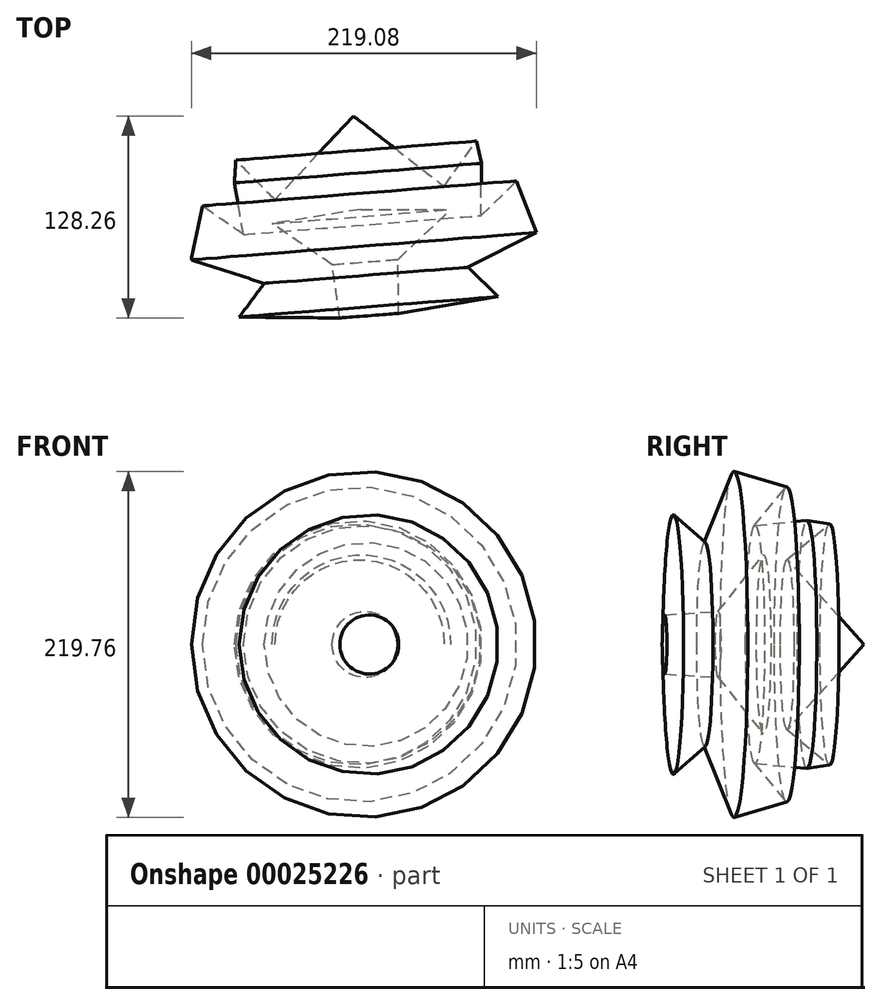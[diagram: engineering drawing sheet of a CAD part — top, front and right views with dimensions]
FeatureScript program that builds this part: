
annotation { "Feature Type Name" : "Feature", "Feature Type Description" : "" }
export const myFeature = defineFeature(function(context is Context, id is Id, definition is map)
    precondition{}
    {
        {
            var Q0;
            Q0=qCreatedBy(makeId("Top.planeOp"),FACE);
            var sketch = newSketch(context, id + "F0", { "sketchPlane" : qUnion([Q0])});
            skLineSegment(sketch, "E0", {"start": v(29.77, 58.92) * mm, "end": v(9.18, 30.14) * mm});
            skLineSegment(sketch, "E1", {"start": v(9.18, 30.14) * mm, "end": v(-48.38, 74.8) * mm});
            skLineSegment(sketch, "E2", {"start": v(-48.38, 74.8) * mm, "end": v(-43.66, 15.5) * mm});
            skLineSegment(sketch, "E3", {"start": v(-43.66, 15.5) * mm, "end": v(13.4, 15.5) * mm});
            skLineSegment(sketch, "E4", {"start": v(13.4, 15.5) * mm, "end": v(-20.1, -16.25) * mm});
            skLineSegment(sketch, "E5", {"start": v(-20.1, -16.25) * mm, "end": v(-19.6, -50.49) * mm});
            skLineSegment(sketch, "E6", {"start": v(-19.6, -50.49) * mm, "end": v(43.42, -39.82) * mm});
            skLineSegment(sketch, "E7", {"start": v(43.42, -39.82) * mm, "end": v(24.31, -21.21) * mm});
            skLineSegment(sketch, "E8", {"start": v(24.31, -21.21) * mm, "end": v(67.73, 0.87) * mm});
            skLineSegment(sketch, "E9", {"start": v(67.73, 0.87) * mm, "end": v(55.32, 33.62) * mm});
            skLineSegment(sketch, "E10", {"start": v(55.32, 33.62) * mm, "end": v(32.5, 11.54) * mm});
            skLineSegment(sketch, "E11", {"start": v(32.5, 11.54) * mm, "end": v(33, 44.78) * mm});
            skLineSegment(sketch, "E12", {"start": v(33, 44.78) * mm, "end": v(29.77, 58.92) * mm});
            skSolve(sketch);
        }
        {
            var Q0;
            Q0=makeQuery(id+"F0.imprint","IMPRINT",FACE,{"disambiguationData":[TD([[makeQuery(id+"F0.imprint","IMPRINT",EDGE,{"derivedFrom":sQuery(id+"F0.wireOp",EDGE,"E0")}),1.0]])]});
            var Q1;
            Q1=sQuery(id+"F0.wireOp",EDGE,"E2");
            revolve(context, id + "F1", {"entities" : qUnion([Q0]), "axis" : qUnion([Q1]), "revolveType" : RevolveType.FULL});
        }
    });
